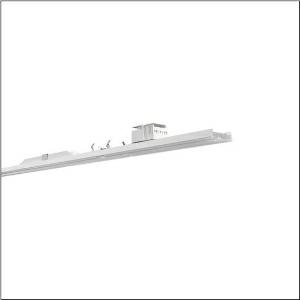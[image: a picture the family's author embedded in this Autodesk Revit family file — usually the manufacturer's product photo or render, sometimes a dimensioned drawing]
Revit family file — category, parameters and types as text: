
# Revit family: licross_r__11_recessed_mo_51tl12dn49xf3c_2425
name_source: partatom
category: Lighting Fixtures
units: mm (PartAtom-declared; Revit-internal decimal feet)

## family parameters
Cut with Voids When Loaded = No
Host = Face
Light Source = No
Part Type = Normal
Room Calculation Point = No
Round Connector Dimension = Use Diameter
Shared = No

## types (1)
- --- (1 x LED, 890 lm, 5 W, 4000K)
    Apparent Load = 5 VA
    CIE Flux Codes = 67 92 99 100 100
    Color Rendering = 80
    Color Temperature = 4000K
    Default Elevation = 1800 mm
    Description = Licross® 11 Recessed MO, luminaire insert, of sheet steel, galvanised, coil coated, white, length: 1.500mm, width: 66mm, height: 67mm, LED rated luminous flux: 9.140lm, light colour: 840, control gear: DALI 2, control gear: ECG DALI, with plug, 6-pole, with phase selection, for trunking rail, 14-core, mains connection: 220..240V, AC/DC, 0/50..60Hz, for emergency light function, halogen-free wiring, charging phase on R (wire number 6), converter,control gear: single battery element, battery: LiFeP04, 9Ah, primary optical cover: cover, of PMMA, light emission: direct distribution, protection rating (complete): IP40, insulation class (complete): insulation class I (protective earthing), certification: CE, UKCA, protection symbol: D if used in an environment without relevant dust loads with corresponding accessories, permissible ambient temperature for indoor applications: +5..+35°C, standard: EN 60598-2-22, corresponds to IFS (International Featured Standards) requirements for safety and quality in the food industry, reducing of maximum allowable ambient temperature of 5°C with ceiling mounting, LABS conformity tested according to VDMA 24364:2018-05, packaging unit: 1 piece
    Height = 58 mm
    Lamp = 1 x LED
    Lamp Light Flux = 890 lm
    Lamp Power = 5 W
    Lamp count = 1
    Length = 1500 mm
    Luminous efficacy = 178 lm/W
    Manufacturer = Siteco
    ModVariant = No
    Model = 51TL12DN49XF3C
    Mounting Place = Ceiling
    Mounting Type = Pendant
    Number of Poles = 1
    OnlyDefault = Yes
    Power Factor = 1
    Product Name = Licross® 11 Recessed MO
    Product group = luminaire insert
    ProductGroupID = 902
    Protection Class = Protection class I
    Protection Degree = IP 40
    RLX_Detail_Level = 1
    RlxData = <blob elided: 22889 chars, md5=36c405d2>
    Socket = socket
    Standby Power = 0 W
    System Light Flux = 890 lm
    System Power = 5 W
    Type Comments = : emergency light operation: 3 h
    Type Image = l_1266722.jpg
    URL = http://relux.com
    VarID = @adj_125905
    Voltage = 0 V
    Weight = 0.00 kg
    Width = 66 mm

## geometry (parser evidence)
native form markers: Blend x4, Sweep x9
no freeform markers — native parametric forms only
